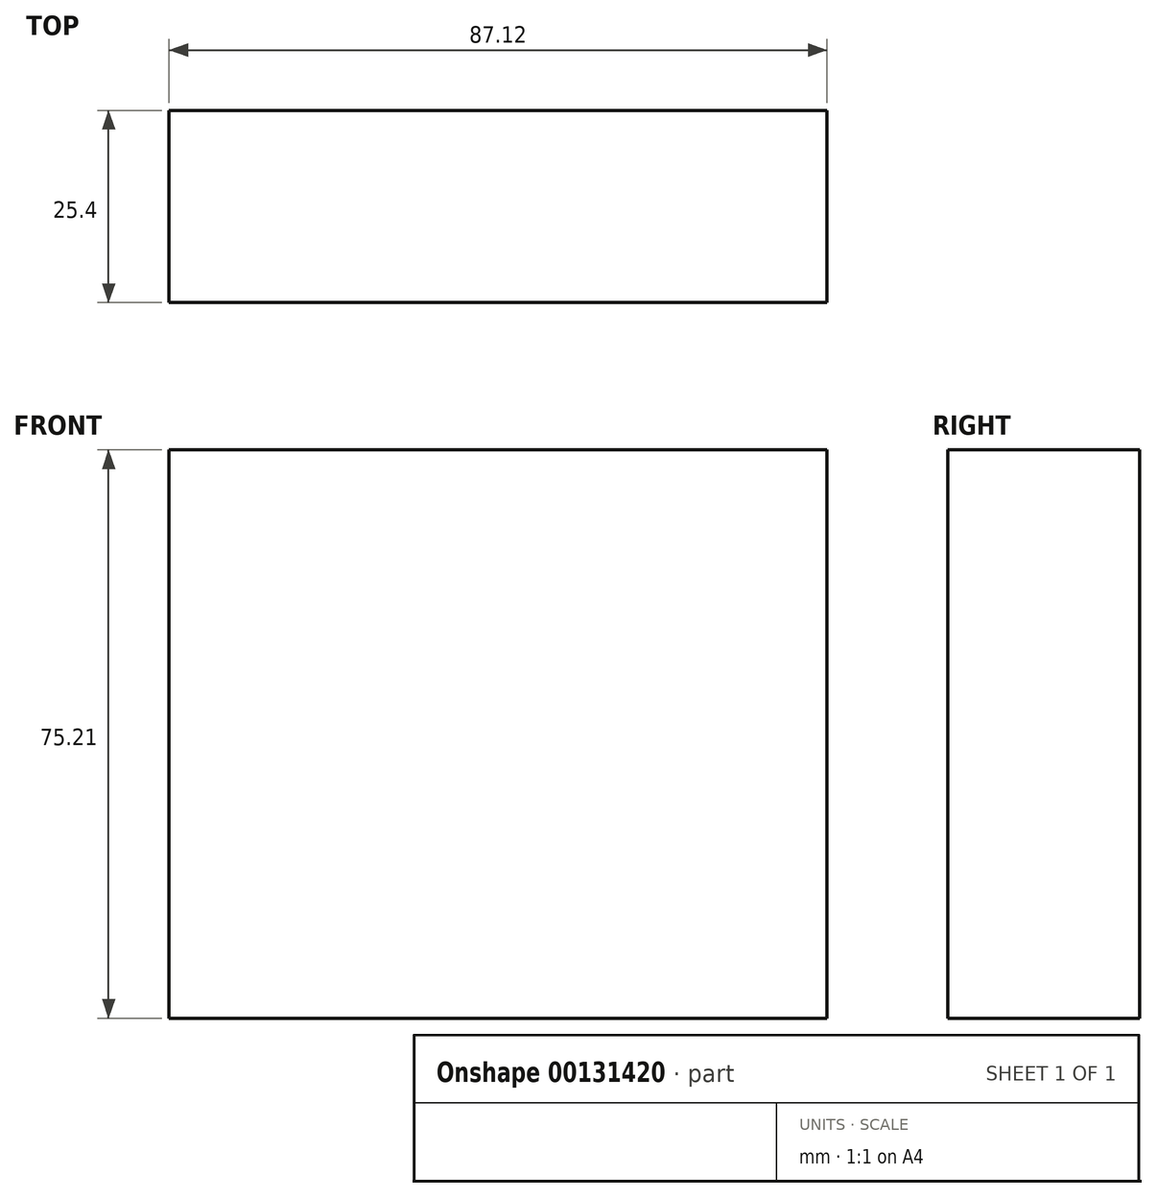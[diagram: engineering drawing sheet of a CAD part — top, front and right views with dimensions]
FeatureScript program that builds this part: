
annotation { "Feature Type Name" : "Feature", "Feature Type Description" : "" }
export const myFeature = defineFeature(function(context is Context, id is Id, definition is map)
    precondition{}
    {
        {
            var Q0;
            Q0=qCreatedBy(makeId("Front.planeOp"),FACE);
            var sketch = newSketch(context, id + "F0", { "sketchPlane" : qUnion([Q0])});
            skLineSegment(sketch, "E0.bottom", {"start": v(-28.46, 16.7) * mm, "end": v(28.46, 16.7) * mm});
            skLineSegment(sketch, "E0.top", {"start": v(-28.46, -33.25) * mm, "end": v(28.46, -33.25) * mm});
            skLineSegment(sketch, "E0.left", {"start": v(-28.46, 16.7) * mm, "end": v(-28.46, -33.25) * mm});
            skLineSegment(sketch, "E0.right", {"start": v(28.46, 16.7) * mm, "end": v(28.46, -33.25) * mm});
            skSolve(sketch);
        }
        {
            var Q0;
            Q0 = qSketchRegion(id + "F0", true);
            extrude(context, id + "F1", {"entities" : qUnion([Q0]), "depth" : 25.4 * mm});
        }
        {
            var Q0;
            Q0=qCreatedBy(makeId("Front.planeOp"),FACE);
            var sketch = newSketch(context, id + "F2", { "sketchPlane" : qUnion([Q0])});
            skLineSegment(sketch, "E1.bottom", {"start": v(-42.98, 26.86) * mm, "end": v(44.14, 26.86) * mm});
            skLineSegment(sketch, "E1.top", {"start": v(-42.98, -48.35) * mm, "end": v(44.14, -48.35) * mm});
            skLineSegment(sketch, "E1.left", {"start": v(-42.98, 26.86) * mm, "end": v(-42.98, -48.35) * mm});
            skLineSegment(sketch, "E1.right", {"start": v(44.14, 26.86) * mm, "end": v(44.14, -48.35) * mm});
            skSolve(sketch);
        }
        {
            var Q0;
            Q0=makeQuery(id+"F2.imprint","IMPRINT",FACE,{"disambiguationData":[TD([[makeQuery(id+"F2.imprint","IMPRINT",EDGE,{"derivedFrom":sQuery(id+"F2.wireOp",EDGE,"E1.bottom")}),-1.0]])]});
            extrude(context, id + "F3", {"entities" : qUnion([Q0]), "operationType" : NewBodyOperationType.ADD, "depth" : 25.4 * mm});
        }
    });
